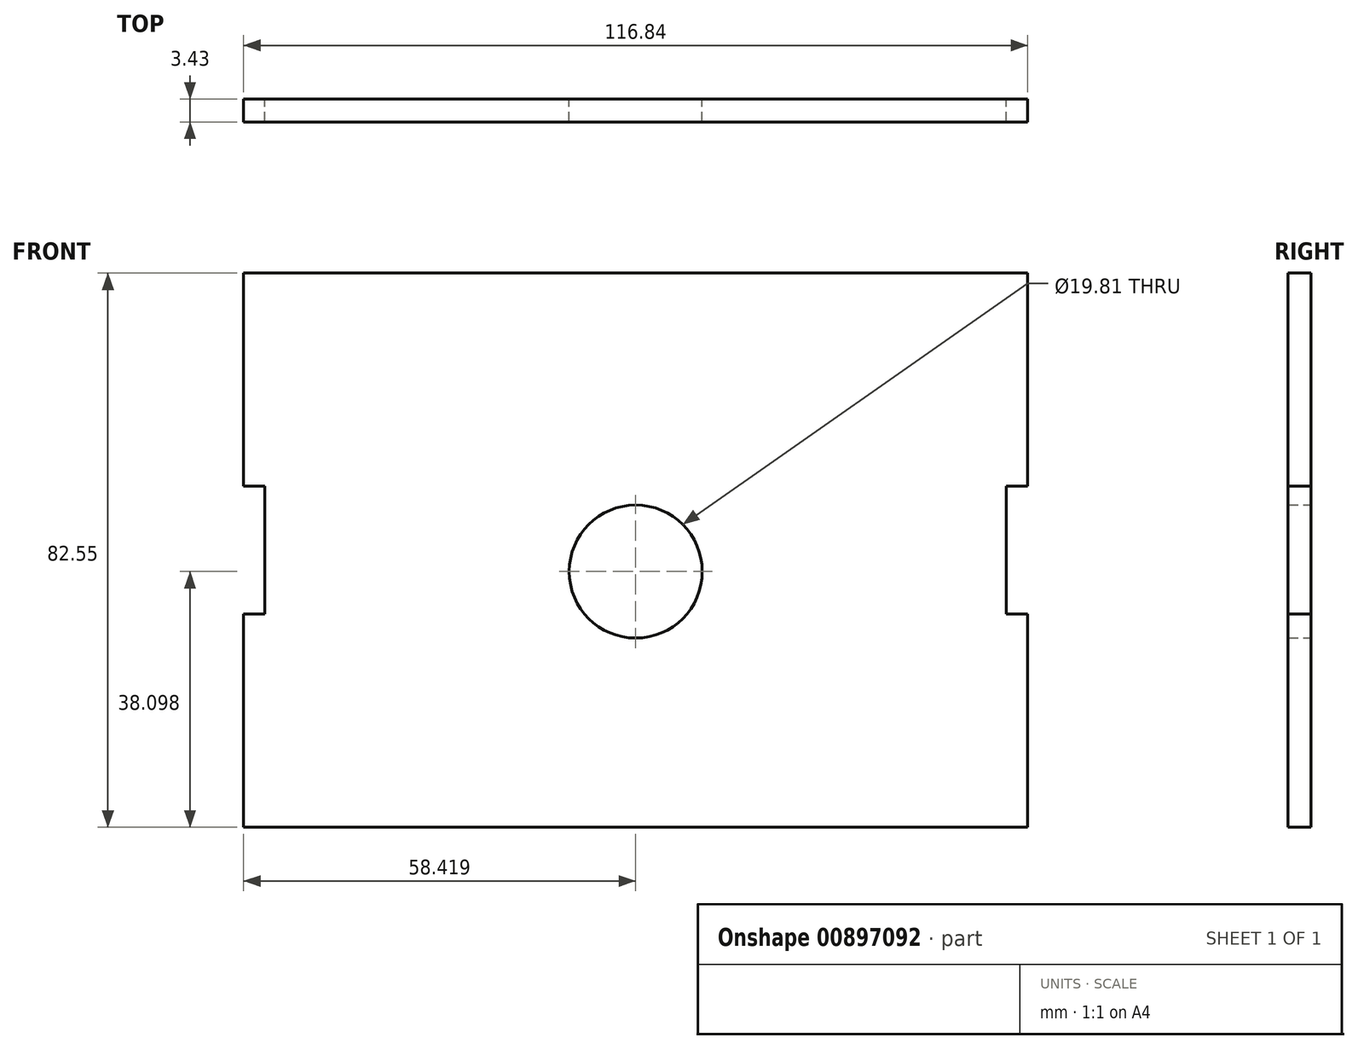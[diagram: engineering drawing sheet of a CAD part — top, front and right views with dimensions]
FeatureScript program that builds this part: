
annotation { "Feature Type Name" : "Feature", "Feature Type Description" : "" }
export const myFeature = defineFeature(function(context is Context, id is Id, definition is map)
    precondition{}
    {
        {
            var Q0;
            Q0=qCreatedBy(makeId("Front.planeOp"),FACE);
            var sketch = newSketch(context, id + "F0", { "sketchPlane" : qUnion([Q0])});
            skCircle(sketch, "E0", {"center": v(480.73, 309.8) * mm, "radius": 9.9 * mm});
            skLineSegment(sketch, "E1", {"start": v(422.3, 271.7) * mm, "end": v(539.15, 271.7) * mm});
            skLineSegment(sketch, "E2", {"start": v(422.3, 303.46) * mm, "end": v(422.3, 271.7) * mm});
            skLineSegment(sketch, "E3", {"start": v(422.3, 303.46) * mm, "end": v(425.48, 303.46) * mm});
            skLineSegment(sketch, "E4", {"start": v(425.48, 303.46) * mm, "end": v(425.48, 322.5) * mm});
            skLineSegment(sketch, "E5", {"start": v(425.48, 322.5) * mm, "end": v(422.3, 322.5) * mm});
            skLineSegment(sketch, "E6", {"start": v(539.15, 354.26) * mm, "end": v(422.3, 354.26) * mm});
            skLineSegment(sketch, "E7", {"start": v(539.15, 322.5) * mm, "end": v(539.15, 354.26) * mm});
            skLineSegment(sketch, "E8", {"start": v(539.15, 322.5) * mm, "end": v(535.97, 322.5) * mm});
            skLineSegment(sketch, "E9", {"start": v(535.97, 322.5) * mm, "end": v(535.97, 303.46) * mm});
            skLineSegment(sketch, "E10", {"start": v(535.97, 303.46) * mm, "end": v(539.15, 303.46) * mm});
            skLineSegment(sketch, "E11", {"start": v(422.3, 354.26) * mm, "end": v(422.3, 322.5) * mm});
            skLineSegment(sketch, "E12", {"start": v(539.15, 271.7) * mm, "end": v(539.15, 303.46) * mm});
            skSolve(sketch);
        }
        {
            var Q0;
            Q0 = qSketchRegion(id + "F0", true);
            extrude(context, id + "F1", {"entities" : qUnion([Q0]), "depth" : 3.43 * mm, "offsetDistance" : 25.4 * mm});
        }
    });
